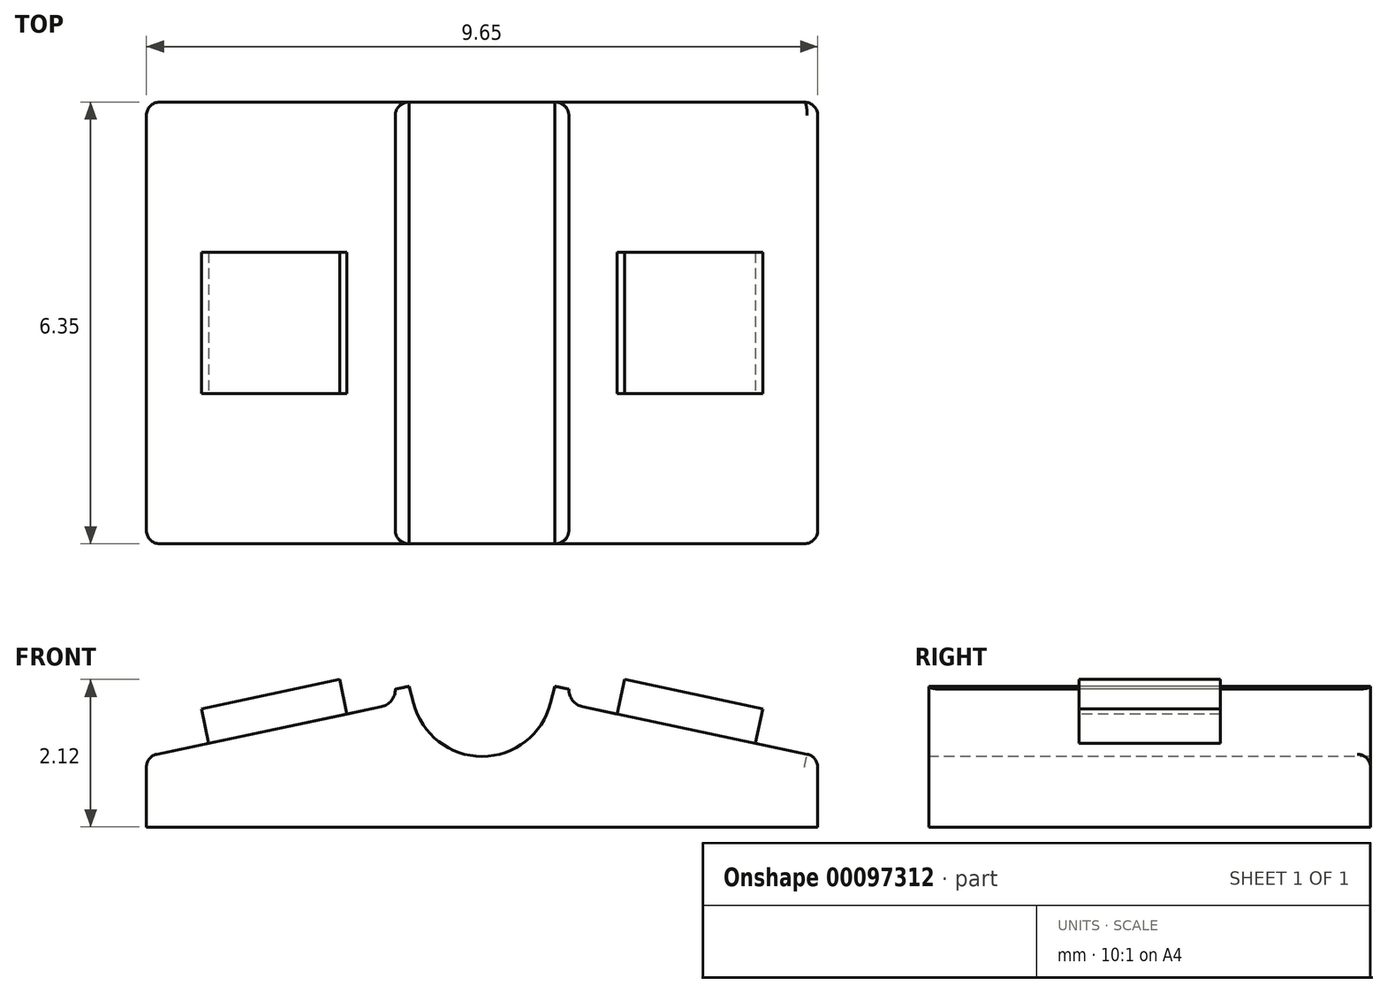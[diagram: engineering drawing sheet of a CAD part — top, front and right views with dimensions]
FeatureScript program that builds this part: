
annotation { "Feature Type Name" : "Feature", "Feature Type Description" : "" }
export const myFeature = defineFeature(function(context is Context, id is Id, definition is map)
    precondition{}
    {
        {
            var Q0;
            Q0=qCreatedBy(makeId("Front.planeOp"),FACE);
            var sketch = newSketch(context, id + "F0", { "sketchPlane" : qUnion([Q0])});
            skLineSegment(sketch, "E0", {"start": v(0, 0) * mm, "end": v(9.65, 0) * mm});
            skLineSegment(sketch, "E1", {"start": v(9.65, 0) * mm, "end": v(9.65, 0.76) * mm});
            skLineSegment(sketch, "E2", {"start": v(0, 0.76) * mm, "end": v(0, 0) * mm});
            skArc(sketch, "E3", {"start": v(3.84, 1.53) * mm, "mid": v(4.83, 0.76) * mm, "end": v(5.81, 1.53) * mm});
            skLineSegment(sketch, "E4", {"start": v(6.02, 1.53) * mm, "end": v(9.65, 0.76) * mm});
            skLineSegment(sketch, "E5", {"start": v(3.63, 1.53) * mm, "end": v(0, 0.76) * mm});
            skLineSegment(sketch, "E6", {"start": v(5.87, 1.77) * mm, "end": v(6.07, 1.73) * mm});
            skLineSegment(sketch, "E7", {"start": v(3.78, 1.77) * mm, "end": v(3.58, 1.73) * mm});
            skLineSegment(sketch, "E8", {"start": v(3.84, 1.53) * mm, "end": v(3.78, 1.77) * mm});
            skLineSegment(sketch, "E9", {"start": v(5.81, 1.53) * mm, "end": v(5.87, 1.77) * mm});
            skLineSegment(sketch, "E10", {"start": v(6.02, 1.53) * mm, "end": v(6.07, 1.73) * mm});
            skLineSegment(sketch, "E11", {"start": v(3.63, 1.53) * mm, "end": v(3.58, 1.73) * mm});
            skSolve(sketch);
        }
        {
            var Q0;
            Q0=makeQuery(id+"F0.imprint","IMPRINT",FACE,{"disambiguationData":[TD([[makeQuery(id+"F0.imprint","IMPRINT",EDGE,{"derivedFrom":sQuery(id+"F0.wireOp",EDGE,"E0")}),1.0]])]});
            extrude(context, id + "F1", {"entities" : qUnion([Q0]), "oppositeDirection" : true, "depth" : 6.35 * mm});
        }
        {
            var Q0;
            Q0=makeQuery(id+"F1.opExtrude","SWEPT_FACE",FACE,{"disambiguationData":[OSD([sQuery(id+"F0.wireOp",EDGE,"E4")])]});
            var sketch = newSketch(context, id + "F2", { "sketchPlane" : qUnion([Q0])});
            skLineSegment(sketch, "E12.bottom", {"start": v(8.37, 4.2) * mm, "end": v(6.34, 4.2) * mm});
            skLineSegment(sketch, "E12.top", {"start": v(8.37, 2.16) * mm, "end": v(6.34, 2.16) * mm});
            skLineSegment(sketch, "E12.left", {"start": v(8.37, 4.2) * mm, "end": v(8.37, 2.16) * mm});
            skLineSegment(sketch, "E12.right", {"start": v(6.34, 4.2) * mm, "end": v(6.34, 2.16) * mm});
            skPoint(sketch, "E12.middle", {"position": v(7.36, 3.18) * mm});
            skSolve(sketch);
        }
        {
            var Q0;
            Q0=qCreatedBy(makeId("Right.planeOp"),FACE);
            cPlane(context, id + "F3", {"entities" : qUnion([Q0]), "cplaneType" : CPlaneType.OFFSET, "offset" : 4.83 * mm, "width" : 152.4 * mm, "height" : 152.4 * mm});
        }
        {
            var Q0;
            Q0=makeQuery(id+"F1.opExtrude","SWEPT_EDGE",EDGE,{"disambiguationData":[OSD([sQuery(id+"F0.wireOp",EDGE,"E4"),sQuery(id+"F0.wireOp",EDGE,"E10")])]});
            var Q1;
            Q1=makeQuery(id+"F1.opExtrude","SWEPT_EDGE",EDGE,{"disambiguationData":[OSD([sQuery(id+"F0.wireOp",EDGE,"E5"),sQuery(id+"F0.wireOp",EDGE,"E11")])]});
            fillet(context, id + "F4", {"entities" : qUnion([Q0, Q1]), "radius" : 0.25 * mm, "tangentPropagation" : true, "allowEdgeOverflow" : false});
        }
        {
            var Q0;
            Q0 = qSketchRegion(id + "F2", true);
            extrude(context, id + "F5", {"entities" : qUnion([Q0]), "operationType" : NewBodyOperationType.ADD, "depth" : 0.5 * mm});
        }
        {
            var Q0;
            Q0=makeQuery(id+"F5.opExtrude","SWEPT_FACE",FACE,{"disambiguationData":[OSD([sQuery(id+"F2.wireOp",EDGE,"E12.top")])]});
            var Q1;
            Q1=makeQuery(id+"F5.opExtrude","SWEPT_FACE",FACE,{"disambiguationData":[OSD([sQuery(id+"F2.wireOp",EDGE,"E12.left")])]});
            var Q2;
            Q2=makeQuery(id+"F5.opExtrude","SWEPT_FACE",FACE,{"disambiguationData":[OSD([sQuery(id+"F2.wireOp",EDGE,"E12.right")])]});
            var Q3;
            Q3=makeQuery(id+"F5.opExtrude","SWEPT_FACE",FACE,{"disambiguationData":[OSD([sQuery(id+"F2.wireOp",EDGE,"E12.bottom")])]});
            var Q4;
            Q4=makeQuery(id+"F5.opExtrude","CAP_FACE",FACE,{"disambiguationData":[OSD([sQuery(id+"F2.wireOp",EDGE,"E12.bottom"),sQuery(id+"F2.wireOp",EDGE,"E12.top"),sQuery(id+"F2.wireOp",EDGE,"E12.left"),sQuery(id+"F2.wireOp",EDGE,"E12.right")])],"isStart":false});
            var Q5;
            Q5=qCreatedBy(id+"F3.planeOp",FACE);
            mirror(context, id + "F6", {"faces" : qUnion([Q0, Q1, Q2, Q3, Q4]), "mirrorPlane" : qUnion([Q5]), "patternType" : MirrorType.FACE});
        }
        {
            var Q0;
            Q0=makeQuery(id+"F1.opExtrude","SWEPT_EDGE",EDGE,{"disambiguationData":[OSD([sQuery(id+"F0.wireOp",EDGE,"E1"),sQuery(id+"F0.wireOp",EDGE,"E4")])]});
            var Q1;
            Q1=makeQuery(id+"F1.opExtrude","SWEPT_EDGE",EDGE,{"disambiguationData":[OSD([sQuery(id+"F0.wireOp",EDGE,"E2"),sQuery(id+"F0.wireOp",EDGE,"E5")])]});
            var Q2;
            Q2=makeQuery(id+"F1.opExtrude","CAP_EDGE",EDGE,{"disambiguationData":[OSD([sQuery(id+"F0.wireOp",EDGE,"E4")])],"isStart":false});
            var Q3;
            Q3=makeQuery(id+"F1.opExtrude","CAP_EDGE",EDGE,{"disambiguationData":[OSD([sQuery(id+"F0.wireOp",EDGE,"E4")])],"isStart":true});
            var Q4;
            Q4=makeQuery(id+"F1.opExtrude","CAP_EDGE",EDGE,{"disambiguationData":[OSD([sQuery(id+"F0.wireOp",EDGE,"E5")])],"isStart":true});
            var Q5;
            Q5=makeQuery(id+"F1.opExtrude","CAP_EDGE",EDGE,{"disambiguationData":[OSD([sQuery(id+"F0.wireOp",EDGE,"E5")])],"isStart":false});
            var Q6;
            Q6=makeQuery(id+"F1.opExtrude","CAP_EDGE",EDGE,{"disambiguationData":[OSD([sQuery(id+"F0.wireOp",EDGE,"E1")])],"isStart":true});
            var Q7;
            Q7=makeQuery(id+"F1.opExtrude","CAP_EDGE",EDGE,{"disambiguationData":[OSD([sQuery(id+"F0.wireOp",EDGE,"E1")])],"isStart":false});
            var Q8;
            Q8=makeQuery(id+"F1.opExtrude","CAP_EDGE",EDGE,{"disambiguationData":[OSD([sQuery(id+"F0.wireOp",EDGE,"E2")])],"isStart":true});
            var Q9;
            Q9=makeQuery(id+"F1.opExtrude","CAP_EDGE",EDGE,{"disambiguationData":[OSD([sQuery(id+"F0.wireOp",EDGE,"E2")])],"isStart":false});
            fillet(context, id + "F7", {"entities" : qUnion([Q0, Q1, Q2, Q3, Q4, Q5, Q6, Q7, Q8, Q9]), "radius" : 0.2 * mm, "tangentPropagation" : true, "allowEdgeOverflow" : false});
        }
        {
            var Q0;
            Q0=makeQuery(id+"F1.opExtrude","SWEPT_BODY",BODY,{"disambiguationData":[OSD([sQuery(id+"F0.wireOp",EDGE,"E0"),sQuery(id+"F0.wireOp",EDGE,"E1"),sQuery(id+"F0.wireOp",EDGE,"E2"),sQuery(id+"F0.wireOp",EDGE,"E3"),sQuery(id+"F0.wireOp",EDGE,"E4"),sQuery(id+"F0.wireOp",EDGE,"E5"),sQuery(id+"F0.wireOp",EDGE,"E6"),sQuery(id+"F0.wireOp",EDGE,"E7"),sQuery(id+"F0.wireOp",EDGE,"E8"),sQuery(id+"F0.wireOp",EDGE,"E9"),sQuery(id+"F0.wireOp",EDGE,"E10"),sQuery(id+"F0.wireOp",EDGE,"E11")])]});
            transform(context, id + "F8", {"entities" : qUnion([Q0]), "transformType" : TransformType.TRANSLATION_3D, "dx" : 0 * mm, "dy" : 0 * mm, "dz" : 0 * mm, "makeCopy" : true});
        }
        {
            var Q0;
            Q0=makeQuery(id+"F8.opPattern","COPY",BODY,{"derivedFrom":makeQuery(id+"F1.opExtrude","SWEPT_BODY",BODY,{"disambiguationData":[OSD([sQuery(id+"F0.wireOp",EDGE,"E0"),sQuery(id+"F0.wireOp",EDGE,"E1"),sQuery(id+"F0.wireOp",EDGE,"E2"),sQuery(id+"F0.wireOp",EDGE,"E3"),sQuery(id+"F0.wireOp",EDGE,"E4"),sQuery(id+"F0.wireOp",EDGE,"E5"),sQuery(id+"F0.wireOp",EDGE,"E6"),sQuery(id+"F0.wireOp",EDGE,"E7"),sQuery(id+"F0.wireOp",EDGE,"E8"),sQuery(id+"F0.wireOp",EDGE,"E9"),sQuery(id+"F0.wireOp",EDGE,"E10"),sQuery(id+"F0.wireOp",EDGE,"E11")])]}),"instanceName":"1"});
            transform(context, id + "F9", {"entities" : qUnion([Q0]), "transformType" : TransformType.TRANSLATION_3D, "dx" : 0 * mm, "dy" : 0 * mm, "dz" : 0 * mm, "makeCopy" : true});
        }
        {
            var Q0;
            Q0=makeQuery(id+"F9.opPattern","COPY",BODY,{"derivedFrom":makeQuery(id+"F8.opPattern","COPY",BODY,{"derivedFrom":makeQuery(id+"F1.opExtrude","SWEPT_BODY",BODY,{"disambiguationData":[OSD([sQuery(id+"F0.wireOp",EDGE,"E0"),sQuery(id+"F0.wireOp",EDGE,"E1"),sQuery(id+"F0.wireOp",EDGE,"E2"),sQuery(id+"F0.wireOp",EDGE,"E3"),sQuery(id+"F0.wireOp",EDGE,"E4"),sQuery(id+"F0.wireOp",EDGE,"E5"),sQuery(id+"F0.wireOp",EDGE,"E6"),sQuery(id+"F0.wireOp",EDGE,"E7"),sQuery(id+"F0.wireOp",EDGE,"E8"),sQuery(id+"F0.wireOp",EDGE,"E9"),sQuery(id+"F0.wireOp",EDGE,"E10"),sQuery(id+"F0.wireOp",EDGE,"E11")])]}),"instanceName":"1"}),"instanceName":"1"});
            deleteBodies(context, id + "F10", {"entities" : qUnion([Q0])});
        }
        {
            var Q0;
            Q0=makeQuery(id+"F8.opPattern","COPY",BODY,{"derivedFrom":makeQuery(id+"F1.opExtrude","SWEPT_BODY",BODY,{"disambiguationData":[OSD([sQuery(id+"F0.wireOp",EDGE,"E0"),sQuery(id+"F0.wireOp",EDGE,"E1"),sQuery(id+"F0.wireOp",EDGE,"E2"),sQuery(id+"F0.wireOp",EDGE,"E3"),sQuery(id+"F0.wireOp",EDGE,"E4"),sQuery(id+"F0.wireOp",EDGE,"E5"),sQuery(id+"F0.wireOp",EDGE,"E6"),sQuery(id+"F0.wireOp",EDGE,"E7"),sQuery(id+"F0.wireOp",EDGE,"E8"),sQuery(id+"F0.wireOp",EDGE,"E9"),sQuery(id+"F0.wireOp",EDGE,"E10"),sQuery(id+"F0.wireOp",EDGE,"E11")])]}),"instanceName":"1"});
            deleteBodies(context, id + "F11", {"entities" : qUnion([Q0])});
        }
        {
            var Q0;
            Q0=makeQuery(id+"F1.opExtrude","SWEPT_FACE",FACE,{"disambiguationData":[OSD([sQuery(id+"F0.wireOp",EDGE,"E0")])]});
            extrude(context, id + "F12", {"entities" : qUnion([Q0]), "operationType" : NewBodyOperationType.ADD, "depth" : 0.25 * mm});
        }
    });
